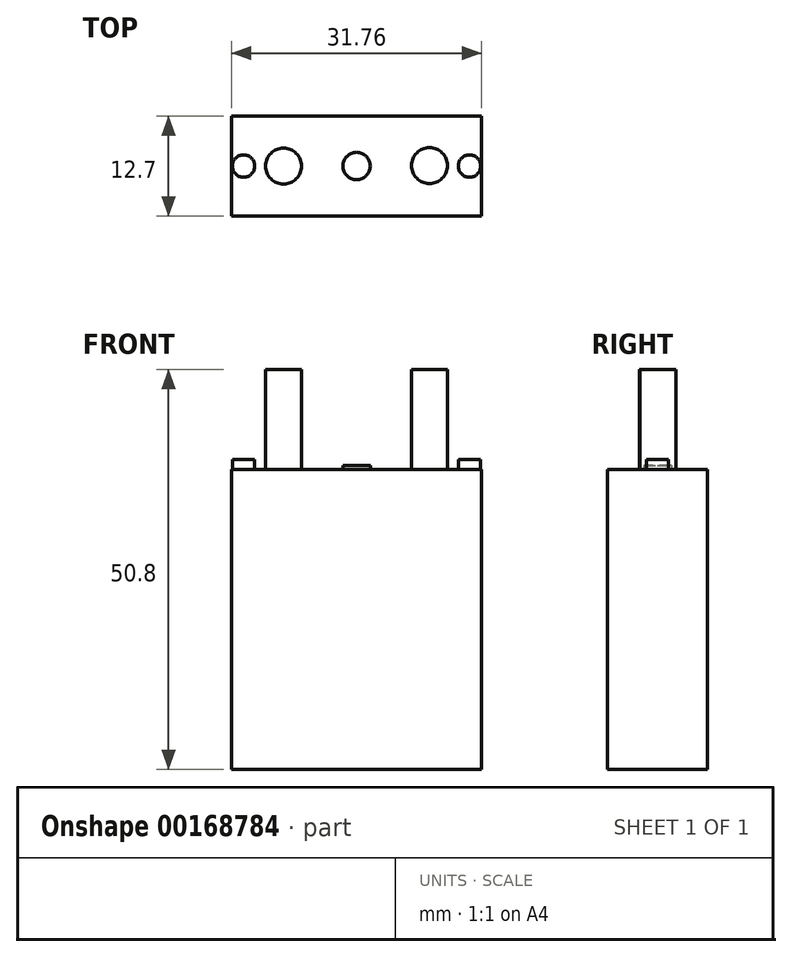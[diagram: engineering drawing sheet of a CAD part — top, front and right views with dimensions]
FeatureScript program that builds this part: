
annotation { "Feature Type Name" : "Feature", "Feature Type Description" : "" }
export const myFeature = defineFeature(function(context is Context, id is Id, definition is map)
    precondition{}
    {
        {
            var Q0;
            Q0=qCreatedBy(makeId("Front.planeOp"),FACE);
            var sketch = newSketch(context, id + "F0", { "sketchPlane" : qUnion([Q0])});
            skLineSegment(sketch, "E0.bottom", {"start": v(15.88, 19.05) * mm, "end": v(-15.88, 19.05) * mm});
            skLineSegment(sketch, "E0.top", {"start": v(15.88, -19.05) * mm, "end": v(-15.88, -19.05) * mm});
            skLineSegment(sketch, "E0.left", {"start": v(15.88, 19.05) * mm, "end": v(15.88, -19.05) * mm});
            skLineSegment(sketch, "E0.right", {"start": v(-15.88, 19.05) * mm, "end": v(-15.88, -19.05) * mm});
            skPoint(sketch, "E0.middle", {"position": v(0, 0) * mm});
            skLineSegment(sketch, "E1", {"start": v(-15.88, 12.7) * mm, "end": v(15.87, 12.7) * mm});
            skLineSegment(sketch, "E2", {"start": v(15.87, 12.7) * mm, "end": v(-15.88, 12.7) * mm});
            skLineSegment(sketch, "E3", {"start": v(-15.88, 6.35) * mm, "end": v(15.87, 6.35) * mm});
            skLineSegment(sketch, "E4", {"start": v(-15.88, 0) * mm, "end": v(15.88, 0) * mm});
            skLineSegment(sketch, "E5", {"start": v(15.88, 0) * mm, "end": v(-15.88, 0) * mm});
            skLineSegment(sketch, "E6", {"start": v(-15.88, -6.35) * mm, "end": v(15.87, -6.35) * mm});
            skLineSegment(sketch, "E7", {"start": v(15.87, -6.35) * mm, "end": v(-15.88, -6.35) * mm});
            skLineSegment(sketch, "E8", {"start": v(-15.88, -12.7) * mm, "end": v(15.87, -12.7) * mm});
            skSolve(sketch);
        }
        {
            var Q0;
            Q0 = qSketchRegion(id + "F0", true);
            extrude(context, id + "F1", {"entities" : qUnion([Q0]), "oppositeDirection" : true, "depth" : 12.7 * mm});
        }
        {
            var Q0;
            Q0=makeQuery(id+"F1.opExtrude","SWEPT_FACE",FACE,{"disambiguationData":[OSD([sQuery(id+"F0.wireOp",EDGE,"E0.bottom")])]});
            var sketch = newSketch(context, id + "F2", { "sketchPlane" : qUnion([Q0])});
            skCircle(sketch, "E9", {"center": v(0, 6.35) * mm, "radius": 1.75 * mm});
            skCircle(sketch, "E10", {"center": v(-14.35, 6.35) * mm, "radius": 1.42 * mm});
            skCircle(sketch, "E11", {"center": v(-9.27, 6.35) * mm, "radius": 2.28 * mm});
            skCircle(sketch, "E12", {"center": v(14.35, 6.35) * mm, "radius": 1.42 * mm});
            skCircle(sketch, "E13", {"center": v(9.27, 6.41) * mm, "radius": 2.28 * mm});
            skSolve(sketch);
        }
        {
            var Q0;
            Q0=makeQuery(id+"F2.imprint","IMPRINT",FACE,{"disambiguationData":[TD([[makeQuery(id+"F2.imprint","IMPRINT",EDGE,{"derivedFrom":sQuery(id+"F2.wireOp",EDGE,"E10")}),1.0]])]});
            var Q1;
            Q1=makeQuery(id+"F2.imprint","IMPRINT",FACE,{"disambiguationData":[TD([[makeQuery(id+"F2.imprint","IMPRINT",EDGE,{"derivedFrom":sQuery(id+"F2.wireOp",EDGE,"E12")}),1.0]])]});
            extrude(context, id + "F3", {"entities" : qUnion([Q0, Q1]), "operationType" : NewBodyOperationType.ADD, "depth" : 1.27 * mm});
        }
        {
            var Q0;
            Q0=makeQuery(id+"F2.imprint","IMPRINT",FACE,{"disambiguationData":[TD([[makeQuery(id+"F2.imprint","IMPRINT",EDGE,{"derivedFrom":sQuery(id+"F2.wireOp",EDGE,"E9")}),1.0]])]});
            extrude(context, id + "F4", {"entities" : qUnion([Q0]), "operationType" : NewBodyOperationType.ADD, "depth" : 0.5 * mm});
        }
        {
            var Q0;
            Q0=sQuery(id+"F0.wireOp",EDGE,"E0.top");
            var Q1;
            Q1=sQuery(id+"F0.wireOp",EDGE,"E8");
            var Q2;
            Q2=sQuery(id+"F0.wireOp",EDGE,"E7");
            var Q3;
            Q3=sQuery(id+"F0.wireOp",EDGE,"E5");
            var Q4;
            Q4=sQuery(id+"F0.wireOp",EDGE,"E3");
            var Q5;
            Q5=sQuery(id+"F0.wireOp",EDGE,"E2");
            var Q6;
            Q6=sQuery(id+"F0.wireOp",EDGE,"E0.bottom");
            extrude(context, id + "F5", {"bodyType" : ToolBodyType.SURFACE, "surfaceEntities" : qUnion([Q0, Q1, Q2, Q3, Q4, Q5, Q6]), "depth" : 0.25 * mm});
        }
        {
            var Q0;
            Q0=makeQuery(id+"F2.imprint","IMPRINT",FACE,{"disambiguationData":[TD([[makeQuery(id+"F2.imprint","IMPRINT",EDGE,{"derivedFrom":sQuery(id+"F2.wireOp",EDGE,"E11")}),1.0]])]});
            var Q1;
            Q1=makeQuery(id+"F2.imprint","IMPRINT",FACE,{"disambiguationData":[TD([[makeQuery(id+"F2.imprint","IMPRINT",EDGE,{"derivedFrom":sQuery(id+"F2.wireOp",EDGE,"E13")}),1.0]])]});
            extrude(context, id + "F6", {"entities" : qUnion([Q0, Q1]), "operationType" : NewBodyOperationType.ADD, "depth" : 12.7 * mm});
        }
    });
